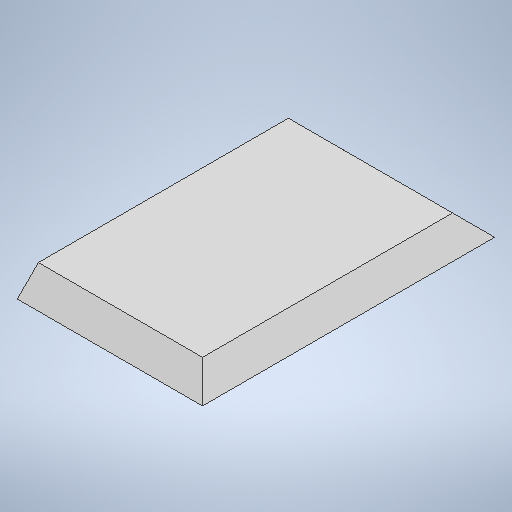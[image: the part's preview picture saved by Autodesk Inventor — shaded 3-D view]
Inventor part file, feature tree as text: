
AUTODESK INVENTOR PART (.ipt)
format: ipt  version: 2025 (Build 290162000, 162)  size: 217,600 bytes
history: native  units: in
note: dims shown in document units (in); Inventor stores cm internally (conversion verified against a paired STEP export)
features: extrude x1, chamfer x1, sketch x1
ambient origin geometry x8: Origin, YZ Plane, XZ Plane, XY Plane, X Axis, Y Axis, Z Axis, Center Point
bodies: Solid1 (feature_tree)
feature tree (3):
  extrude  "Extrusion1"  Depth=0.7874in
  chamfer  "Chamfer3"  Distance=0.7874in
  sketch  "Sketch1"  dims[d0=6.9252in d1=10.9252in d2=0.7874in d3=0.0in d10=0.7874in d11=0.0492in d12=45.0deg]
